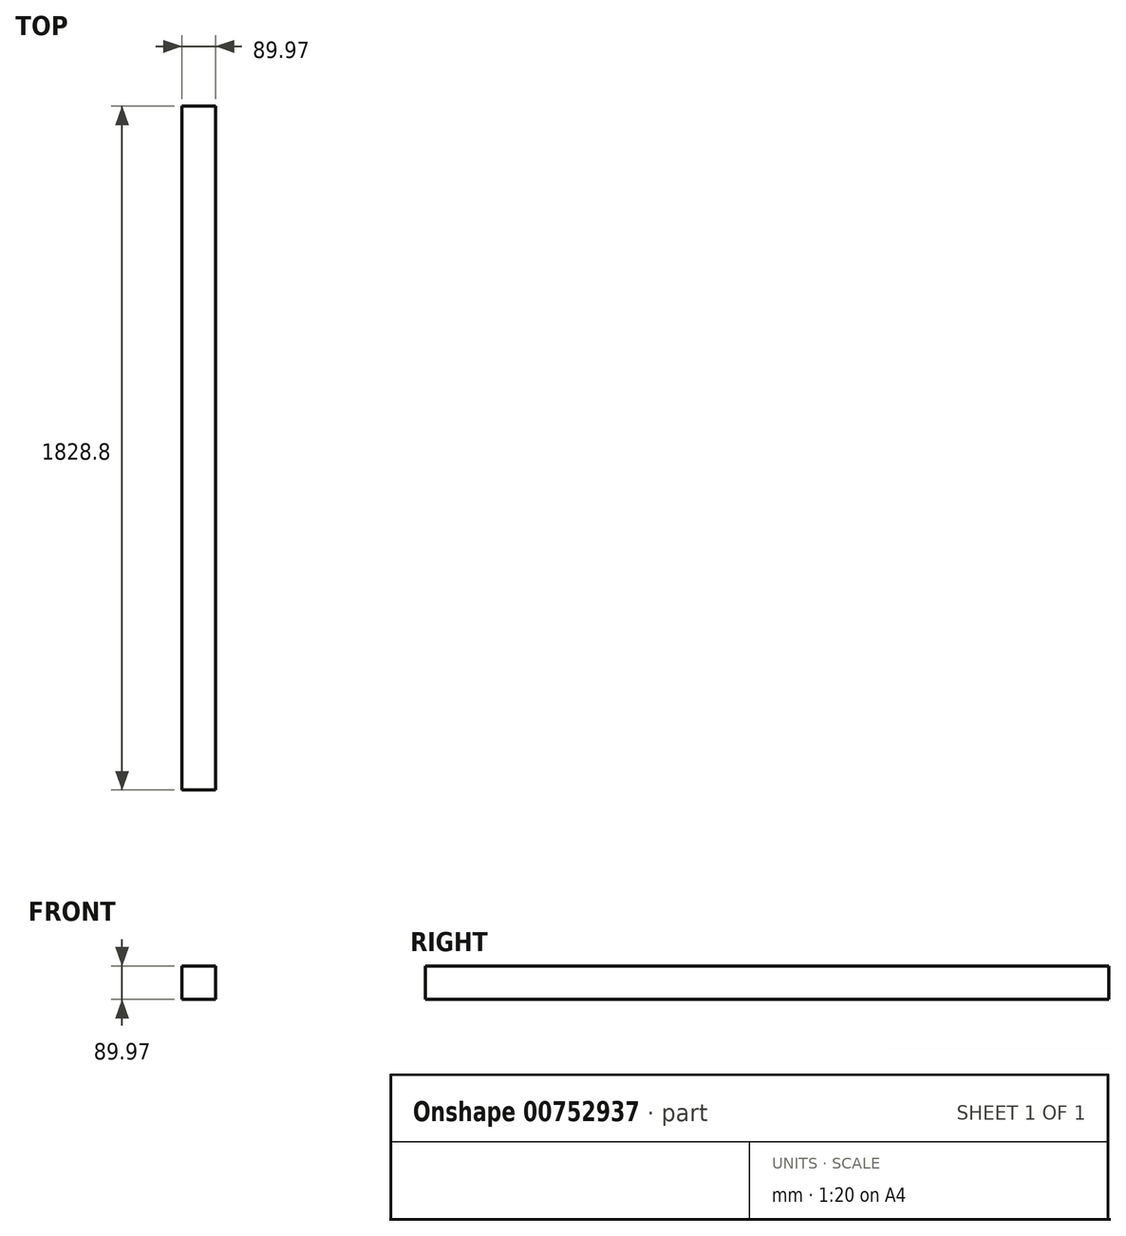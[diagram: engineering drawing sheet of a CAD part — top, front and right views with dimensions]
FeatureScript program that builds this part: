
annotation { "Feature Type Name" : "Feature", "Feature Type Description" : "" }
export const myFeature = defineFeature(function(context is Context, id is Id, definition is map)
    precondition{}
    {
        {
            var Q0;
            Q0=qCreatedBy(makeId("Front.planeOp"),FACE);
            var sketch = newSketch(context, id + "F0", { "sketchPlane" : qUnion([Q0])});
            skLineSegment(sketch, "E0.bottom", {"start": v(10.82, -102.84) * mm, "end": v(-79.15, -102.84) * mm});
            skLineSegment(sketch, "E0.top", {"start": v(10.82, -12.87) * mm, "end": v(-79.15, -12.87) * mm});
            skLineSegment(sketch, "E0.left", {"start": v(10.82, -102.84) * mm, "end": v(10.82, -12.87) * mm});
            skLineSegment(sketch, "E0.right", {"start": v(-79.15, -102.84) * mm, "end": v(-79.15, -12.87) * mm});
            skPoint(sketch, "E0.middle", {"position": v(-34.17, -57.85) * mm});
            skSolve(sketch);
        }
        {
            var Q0;
            Q0=makeQuery(id+"F0.imprint","IMPRINT",FACE,{"disambiguationData":[TD([[makeQuery(id+"F0.imprint","IMPRINT",EDGE,{"derivedFrom":sQuery(id+"F0.wireOp",EDGE,"E0.bottom")}),-1.0]])]});
            extrude(context, id + "F1", {"entities" : qUnion([Q0]), "depth" : 1828.8 * mm, "offsetDistance" : 25.4 * mm});
        }
    });
